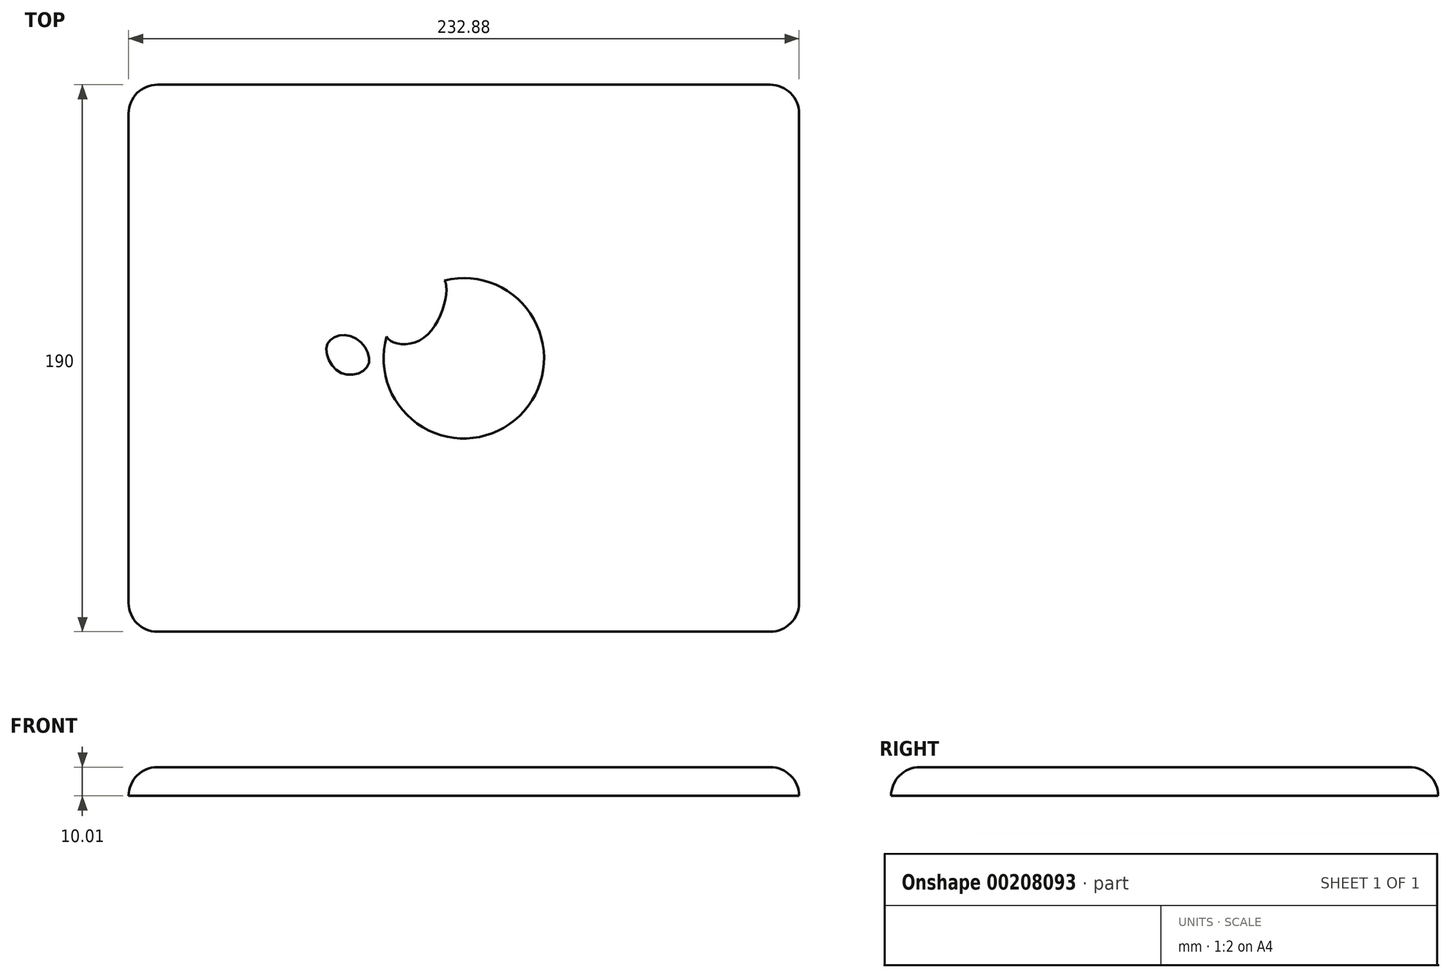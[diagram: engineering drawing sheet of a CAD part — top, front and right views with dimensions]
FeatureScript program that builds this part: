
annotation { "Feature Type Name" : "Feature", "Feature Type Description" : "" }
export const myFeature = defineFeature(function(context is Context, id is Id, definition is map)
    precondition{}
    {
        {
            var Q0;
            Q0=qCreatedBy(makeId("Top.planeOp"),FACE);
            var sketch = newSketch(context, id + "F0", { "sketchPlane" : qUnion([Q0])});
            skLineSegment(sketch, "E0.bottom", {"start": v(-116.44, -94.46) * mm, "end": v(116.44, -94.46) * mm});
            skLineSegment(sketch, "E0.top", {"start": v(-116.44, -284.46) * mm, "end": v(116.44, -284.46) * mm});
            skLineSegment(sketch, "E0.left", {"start": v(-116.44, -94.46) * mm, "end": v(-116.44, -284.46) * mm});
            skLineSegment(sketch, "E0.right", {"start": v(116.44, -94.46) * mm, "end": v(116.44, -284.46) * mm});
            skPoint(sketch, "E0.middle", {"position": v(0, -189.46) * mm});
            skSolve(sketch);
        }
        {
            var Q0;
            Q0 = qSketchRegion(id + "F0", true);
            extrude(context, id + "F1", {"entities" : qUnion([Q0]), "depth" : 10 * mm});
        }
        {
            var Q0;
            Q0=makeQuery(id+"F1.opExtrude","CAP_EDGE",EDGE,{"disambiguationData":[OSD([sQuery(id+"F0.wireOp",EDGE,"E0.bottom")])],"isStart":false});
            var Q1;
            Q1=makeQuery(id+"F1.opExtrude","CAP_EDGE",EDGE,{"disambiguationData":[OSD([sQuery(id+"F0.wireOp",EDGE,"E0.left")])],"isStart":false});
            var Q2;
            Q2=makeQuery(id+"F1.opExtrude","CAP_EDGE",EDGE,{"disambiguationData":[OSD([sQuery(id+"F0.wireOp",EDGE,"E0.right")])],"isStart":false});
            var Q3;
            Q3=makeQuery(id+"F1.opExtrude","CAP_EDGE",EDGE,{"disambiguationData":[OSD([sQuery(id+"F0.wireOp",EDGE,"E0.top")])],"isStart":false});
            fillet(context, id + "F2", {"entities" : qUnion([Q0, Q1, Q2, Q3]), "radius" : 10 * mm, "tangentPropagation" : true, "allowEdgeOverflow" : false});
        }
        {
            var Q0;
            Q0=makeQuery(id+"F2.opFillet","BLEND_EDGE",EDGE,{"blendedFrom":[makeQuery(id+"F1.opExtrude","CAP_EDGE",EDGE,{"disambiguationData":[OSD([sQuery(id+"F0.wireOp",EDGE,"E0.top")])],"isStart":false}),makeQuery(id+"F1.opExtrude","CAP_EDGE",EDGE,{"disambiguationData":[OSD([sQuery(id+"F0.wireOp",EDGE,"E0.right")])],"isStart":false})],"blendedInto":[]});
            var Q1;
            Q1=makeQuery(id+"F2.opFillet","BLEND_EDGE",EDGE,{"blendedFrom":[makeQuery(id+"F1.opExtrude","CAP_EDGE",EDGE,{"disambiguationData":[OSD([sQuery(id+"F0.wireOp",EDGE,"E0.top")])],"isStart":false}),makeQuery(id+"F1.opExtrude","CAP_EDGE",EDGE,{"disambiguationData":[OSD([sQuery(id+"F0.wireOp",EDGE,"E0.left")])],"isStart":false})],"blendedInto":[]});
            var Q2;
            Q2=makeQuery(id+"F2.opFillet","BLEND_EDGE",EDGE,{"blendedFrom":[makeQuery(id+"F1.opExtrude","CAP_EDGE",EDGE,{"disambiguationData":[OSD([sQuery(id+"F0.wireOp",EDGE,"E0.bottom")])],"isStart":false}),makeQuery(id+"F1.opExtrude","CAP_EDGE",EDGE,{"disambiguationData":[OSD([sQuery(id+"F0.wireOp",EDGE,"E0.right")])],"isStart":false})],"blendedInto":[]});
            var Q3;
            Q3=makeQuery(id+"F2.opFillet","BLEND_EDGE",EDGE,{"blendedFrom":[makeQuery(id+"F1.opExtrude","CAP_EDGE",EDGE,{"disambiguationData":[OSD([sQuery(id+"F0.wireOp",EDGE,"E0.bottom")])],"isStart":false}),makeQuery(id+"F1.opExtrude","CAP_EDGE",EDGE,{"disambiguationData":[OSD([sQuery(id+"F0.wireOp",EDGE,"E0.left")])],"isStart":false})],"blendedInto":[]});
            fillet(context, id + "F3", {"entities" : qUnion([Q0, Q1, Q2, Q3]), "radius" : 10 * mm, "tangentPropagation" : true, "allowEdgeOverflow" : false});
        }
        {
            var Q0;
            Q0=makeQuery(id+"F1.opExtrude","CAP_FACE",FACE,{"disambiguationData":[OSD([sQuery(id+"F0.wireOp",EDGE,"E0.bottom"),sQuery(id+"F0.wireOp",EDGE,"E0.top"),sQuery(id+"F0.wireOp",EDGE,"E0.left"),sQuery(id+"F0.wireOp",EDGE,"E0.right")])],"isStart":false});
            var sketch = newSketch(context, id + "F4", { "sketchPlane" : qUnion([Q0])});
            skCircle(sketch, "E1", {"center": v(0, -189.46) * mm, "radius": 27.86 * mm});
            skPoint(sketch, "E1.centerSnap0", {"position": v(-106.44, -189.46) * mm});
            skFitSpline(sketch, "E2", {"points": [v(-16.64, -167.12) * mm, v(-26.8, -181.88) * mm, v(-13.54, -182.13) * mm, v(-6.71, -162.42) * mm, v(-16.64, -167.12) * mm]});
            skFitSpline(sketch, "E3", {"points": [v(-47.36, -184.5) * mm, v(-38.46, -182.13) * mm, v(-33.12, -191.62) * mm, v(-42.61, -194.59) * mm, v(-47.36, -184.5) * mm]});
            skSolve(sketch);
        }
        {
            var Q0;
            {var subQ0=sQuery(id+"F4.wireOp",EDGE,"E2");var subQ1=sQuery(id+"F4.wireOp",EDGE,"E1");var subQ2=makeQuery(id+"F4.imprint","INTERSECT",VERTEX,{"disambiguationData":[OD(1.0)],"derivedFrom":[subQ1,subQ0]});Q0=makeQuery(id+"F4.imprint","IMPRINT",FACE,{"disambiguationData":[TD([[makeQuery(id+"F4.imprint","IMPRINT",EDGE,{"disambiguationData":[TD([[subQ2,1.0]])],"derivedFrom":subQ1}),1.0]])]});}
            var Q1;
            Q1=makeQuery(id+"F4.imprint","IMPRINT",FACE,{"disambiguationData":[TD([[makeQuery(id+"F4.imprint","IMPRINT",EDGE,{"derivedFrom":sQuery(id+"F4.wireOp",EDGE,"E3")}),-1.0]])]});
            extrude(context, id + "F5", {"entities" : qUnion([Q0, Q1]), "operationType" : NewBodyOperationType.ADD, "depth" : 0.01 * mm});
        }
    });
